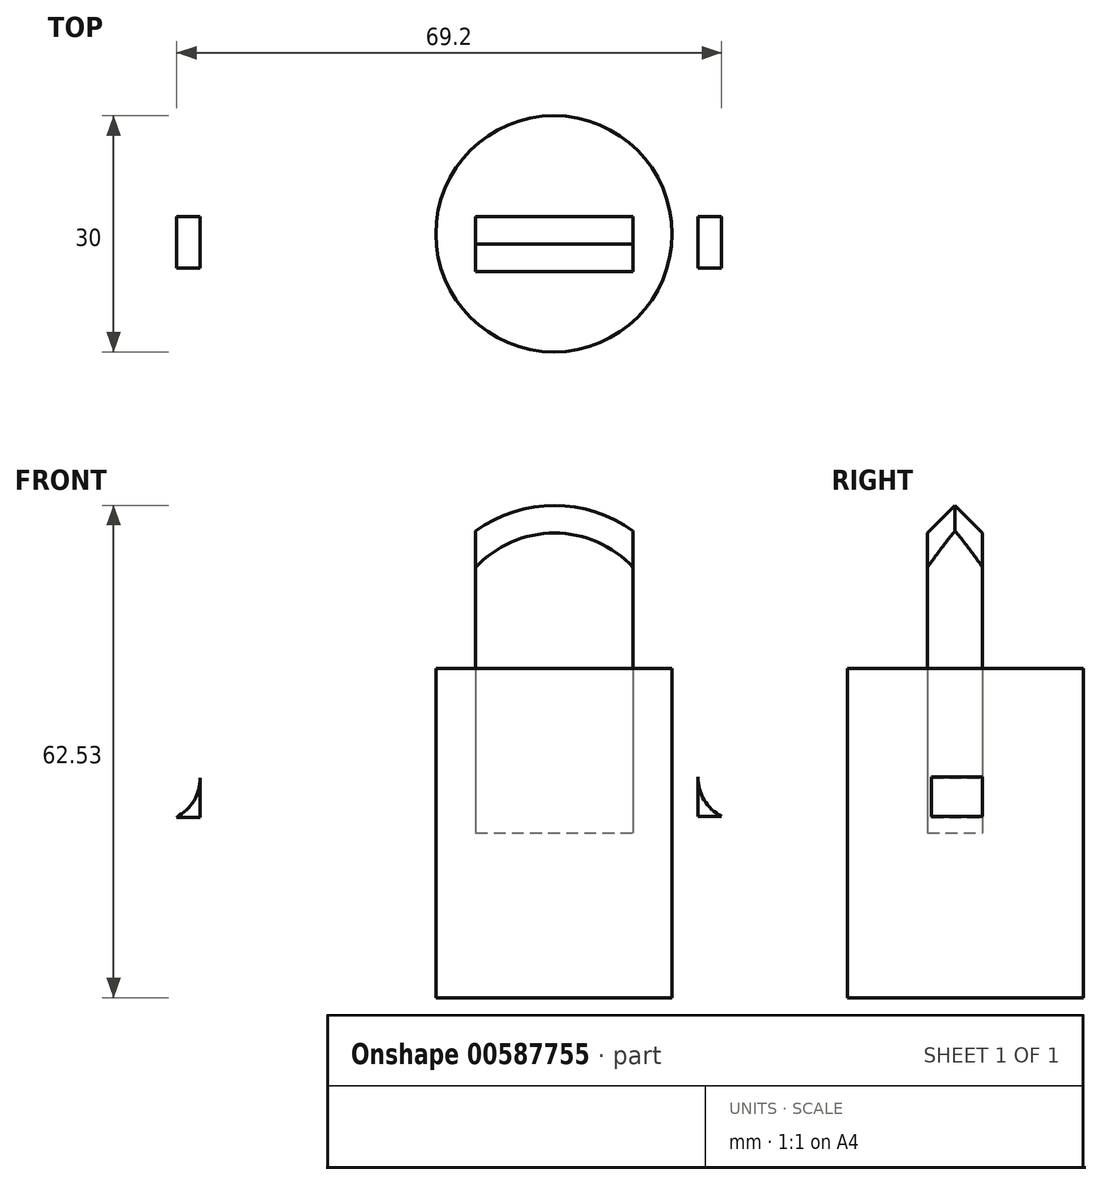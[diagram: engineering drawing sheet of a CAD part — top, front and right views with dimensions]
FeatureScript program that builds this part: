
annotation { "Feature Type Name" : "Feature", "Feature Type Description" : "" }
export const myFeature = defineFeature(function(context is Context, id is Id, definition is map)
    precondition{}
    {
        {
            var Q0;
            Q0=qCreatedBy(makeId("Front.planeOp"),FACE);
            var sketch = newSketch(context, id + "F0", { "sketchPlane" : qUnion([Q0])});
            skLineSegment(sketch, "E0.top", {"start": v(-10, -20.9) * mm, "end": v(10, -20.9) * mm});
            skLineSegment(sketch, "E0.left", {"start": v(-10, 20.9) * mm, "end": v(-10, -20.9) * mm});
            skLineSegment(sketch, "E0.right", {"start": v(10, 20.9) * mm, "end": v(10, -20.9) * mm});
            skPoint(sketch, "E0.middle", {"position": v(0, 0) * mm});
            skArc(sketch, "E1", {"start": v(10, 17.5) * mm, "mid": v(0, 20.73) * mm, "end": v(-10, 17.5) * mm});
            skSolve(sketch);
        }
        {
            var Q0;
            {var subQ0=sQuery(id+"F0.wireOp",EDGE,"E0.top");Q0=makeQuery(id+"F0.imprint","IMPRINT",FACE,{"disambiguationData":[TD([[makeQuery(id+"F0.imprint","IMPRINT",EDGE,{"derivedFrom":subQ0}),1.0]])]});}
            var Q1;
            Q1=sQuery(id+"F0.wireOp",EDGE,"E0.top");
            extrude(context, id + "F1", {"entities" : qUnion([Q0]), "surfaceEntities" : qUnion([Q1]), "depth" : 7 * mm, "offsetDistance" : 25 * mm});
        }
        {
            var Q0;
            Q0=makeQuery(id+"F1.opExtrude","CAP_EDGE",EDGE,{"disambiguationData":[OSD([sQuery(id+"F0.wireOp",EDGE,"E1")])],"isStart":false});
            chamfer(context, id + "F2", {"entities" : qUnion([Q0]), "chamferType" : ChamferType.OFFSET_ANGLE, "width" : 3.5 * mm, "oppositeDirection" : false, "angle" : 45 * degree, "tangentPropagation" : true});
        }
        {
            var Q0;
            Q0=makeQuery(id+"F1.opExtrude","CAP_EDGE",EDGE,{"disambiguationData":[OSD([sQuery(id+"F0.wireOp",EDGE,"E1")])],"isStart":true});
            chamfer(context, id + "F3", {"entities" : qUnion([Q0]), "width" : 3.5 * mm, "tangentPropagation" : true});
        }
        {
            var Q0;
            Q0=qCreatedBy(makeId("Top.planeOp"),FACE);
            var sketch = newSketch(context, id + "F4", { "sketchPlane" : qUnion([Q0])});
            skCircle(sketch, "E2", {"center": v(-0.06, -2.18) * mm, "radius": 15 * mm});
            skSolve(sketch);
        }
        {
            var Q0;
            Q0=makeQuery(id+"F4.imprint","IMPRINT",FACE,{"disambiguationData":[TD([[makeQuery(id+"F4.imprint","IMPRINT",EDGE,{"derivedFrom":sQuery(id+"F4.wireOp",EDGE,"E2")}),1.0]])]});
            extrude(context, id + "F5", {"entities" : qUnion([Q0]), "oppositeDirection" : true, "depth" : 41.8 * mm, "offsetDistance" : 25 * mm});
        }
        {
            var Q0;
            Q0=qCreatedBy(makeId("Front.planeOp"),FACE);
            var sketch = newSketch(context, id + "F6", { "sketchPlane" : qUnion([Q0])});
            skLineSegment(sketch, "E3.bottom", {"start": v(-48, -18.87) * mm, "end": v(-45, -18.87) * mm});
            skLineSegment(sketch, "E3.right", {"start": v(-45, -18.87) * mm, "end": v(-45, -13.87) * mm});
            skArc(sketch, "E4", {"start": v(-48, -18.87) * mm, "mid": v(-45.8, -16.79) * mm, "end": v(-45, -13.87) * mm});
            skSolve(sketch);
        }
        {
            var Q0;
            Q0=qCreatedBy(makeId("Front.planeOp"),FACE);
            var sketch = newSketch(context, id + "F7", { "sketchPlane" : qUnion([Q0])});
            skLineSegment(sketch, "E5.bottom", {"start": v(18.2, -18.77) * mm, "end": v(21.2, -18.77) * mm});
            skLineSegment(sketch, "E5.left", {"start": v(18.2, -18.77) * mm, "end": v(18.2, -13.77) * mm});
            skArc(sketch, "E6", {"start": v(18.2, -13.77) * mm, "mid": v(19.02, -16.68) * mm, "end": v(21.2, -18.77) * mm});
            skSolve(sketch);
        }
        {
            var Q0;
            Q0=makeQuery(id+"F7.imprint","IMPRINT",FACE,{"disambiguationData":[TD([[makeQuery(id+"F7.imprint","IMPRINT",EDGE,{"derivedFrom":sQuery(id+"F7.wireOp",EDGE,"E5.bottom")}),1.0]])]});
            extrude(context, id + "F8", {"entities" : qUnion([Q0]), "depth" : 6.5 * mm, "offsetDistance" : 25 * mm});
        }
        {
            var Q0;
            Q0=makeQuery(id+"F6.imprint","IMPRINT",FACE,{"disambiguationData":[TD([[makeQuery(id+"F6.imprint","IMPRINT",EDGE,{"derivedFrom":sQuery(id+"F6.wireOp",EDGE,"E3.bottom")}),1.0]])]});
            extrude(context, id + "F9", {"entities" : qUnion([Q0]), "depth" : 6.5 * mm, "offsetDistance" : 25 * mm});
        }
    });
